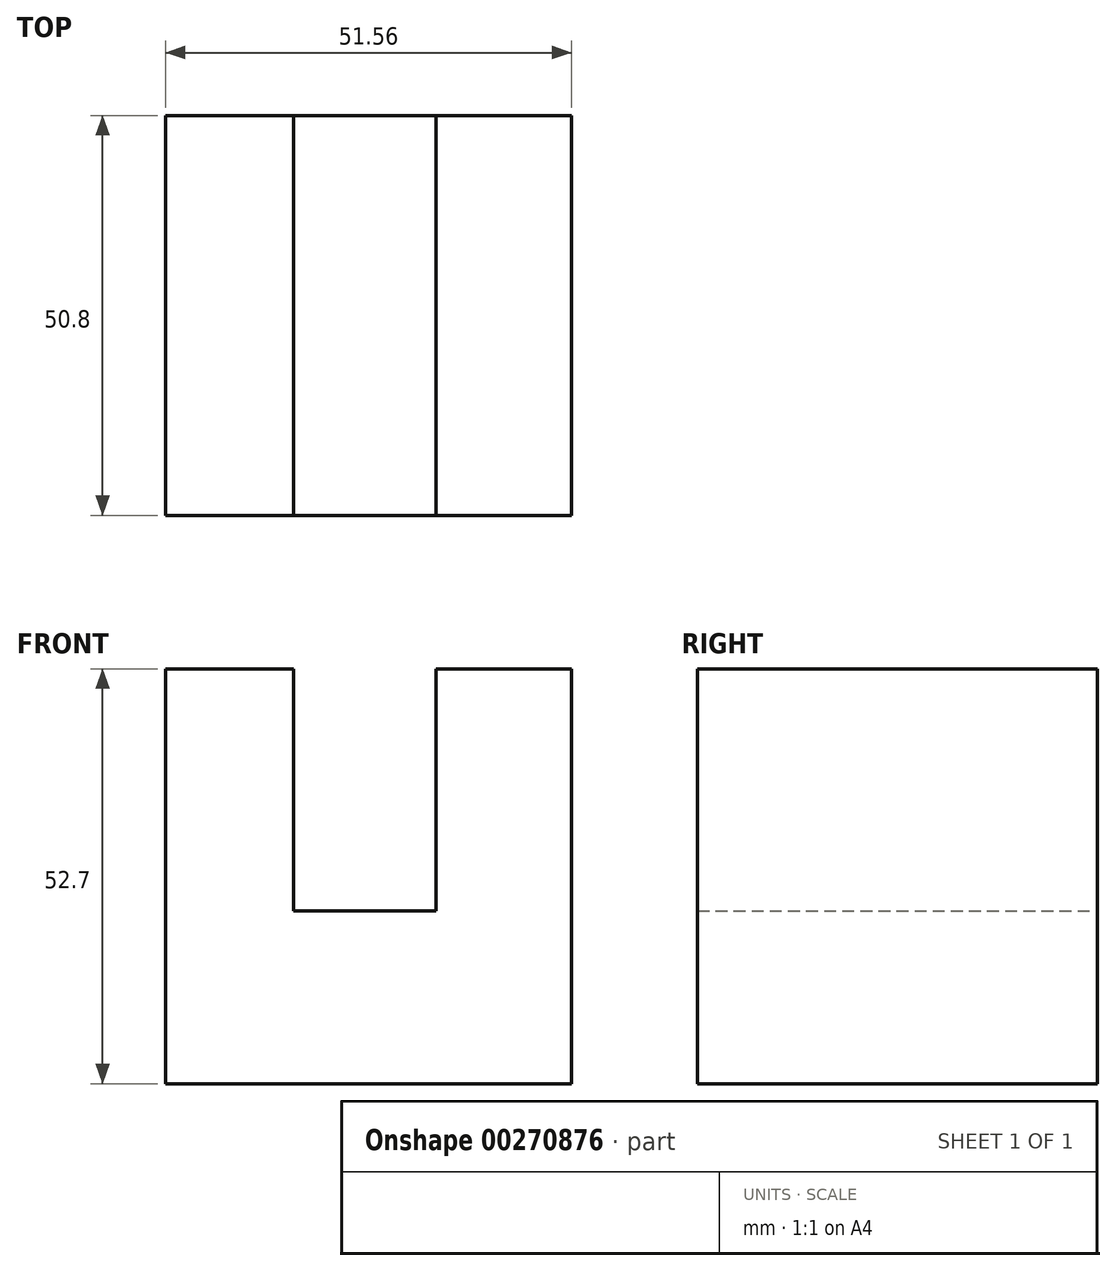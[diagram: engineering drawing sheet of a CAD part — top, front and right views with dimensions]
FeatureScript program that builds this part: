
annotation { "Feature Type Name" : "Feature", "Feature Type Description" : "" }
export const myFeature = defineFeature(function(context is Context, id is Id, definition is map)
    precondition{}
    {
        {
            var Q0;
            Q0=qCreatedBy(makeId("Front.planeOp"),FACE);
            var sketch = newSketch(context, id + "F0", { "sketchPlane" : qUnion([Q0])});
            skLineSegment(sketch, "E0.bottom", {"start": v(-55.19, 0) * mm, "end": v(-55.38, 0) * mm});
            skLineSegment(sketch, "E0.top", {"start": v(-55.19, 52.7) * mm, "end": v(-55.38, 52.7) * mm});
            skLineSegment(sketch, "E0.left", {"start": v(-55.19, 0) * mm, "end": v(-55.19, 52.7) * mm});
            skLineSegment(sketch, "E0.right", {"start": v(-55.38, 0) * mm, "end": v(-55.38, 52.7) * mm});
            skLineSegment(sketch, "E1.bottom", {"start": v(-55.19, 52.7) * mm, "end": v(-38.95, 52.7) * mm});
            skLineSegment(sketch, "E1.top", {"start": v(-55.19, 52.7) * mm, "end": v(-38.95, 52.7) * mm});
            skLineSegment(sketch, "E1.left", {"start": v(-55.19, 52.7) * mm, "end": v(-55.19, 52.7) * mm});
            skLineSegment(sketch, "E1.right", {"start": v(-38.95, 52.7) * mm, "end": v(-38.95, 52.7) * mm});
            skLineSegment(sketch, "E2.bottom", {"start": v(-38.95, 21.96) * mm, "end": v(-38.95, 21.96) * mm});
            skLineSegment(sketch, "E2.left", {"start": v(-38.95, 21.96) * mm, "end": v(-38.95, 52.7) * mm});
            skLineSegment(sketch, "E2.right", {"start": v(-38.95, 21.96) * mm, "end": v(-38.95, 52.7) * mm});
            skLineSegment(sketch, "E3.bottom", {"start": v(-38.95, 21.96) * mm, "end": v(-20.81, 21.96) * mm});
            skLineSegment(sketch, "E3.top", {"start": v(-38.95, 21.96) * mm, "end": v(-20.81, 21.96) * mm});
            skLineSegment(sketch, "E3.right", {"start": v(-20.81, 21.96) * mm, "end": v(-20.81, 21.96) * mm});
            skLineSegment(sketch, "E4.top", {"start": v(-20.81, 52.7) * mm, "end": v(-20.81, 52.7) * mm});
            skLineSegment(sketch, "E4.left", {"start": v(-20.81, 21.96) * mm, "end": v(-20.81, 52.7) * mm});
            skLineSegment(sketch, "E4.right", {"start": v(-20.81, 21.96) * mm, "end": v(-20.81, 52.7) * mm});
            skLineSegment(sketch, "E5.bottom", {"start": v(-3.63, 52.7) * mm, "end": v(-20.81, 52.7) * mm});
            skLineSegment(sketch, "E5.top", {"start": v(-3.63, 52.7) * mm, "end": v(-20.81, 52.7) * mm});
            skLineSegment(sketch, "E5.left", {"start": v(-3.63, 52.7) * mm, "end": v(-3.63, 52.7) * mm});
            skLineSegment(sketch, "E6.bottom", {"start": v(-3.63, 0) * mm, "end": v(-3.63, 0) * mm});
            skLineSegment(sketch, "E6.left", {"start": v(-3.63, 0) * mm, "end": v(-3.63, 52.7) * mm});
            skLineSegment(sketch, "E6.right", {"start": v(-3.63, 0) * mm, "end": v(-3.63, 52.7) * mm});
            skLineSegment(sketch, "E7", {"start": v(-55.38, 0) * mm, "end": v(-3.63, 0) * mm});
            skSolve(sketch);
        }
        {
            var Q0;
            Q0=qCreatedBy(makeId("Front.planeOp"),FACE);
            var sketch = newSketch(context, id + "F1", { "sketchPlane" : qUnion([Q0])});
            skLineSegment(sketch, "E8.bottom", {"start": v(-55.19, 0) * mm, "end": v(-3.44, 0) * mm});
            skLineSegment(sketch, "E8.top", {"start": v(-55.19, 0) * mm, "end": v(-3.44, 0) * mm});
            skLineSegment(sketch, "E8.left", {"start": v(-55.19, 0) * mm, "end": v(-55.19, 0) * mm});
            skLineSegment(sketch, "E8.right", {"start": v(-3.44, 0) * mm, "end": v(-3.44, 0) * mm});
            skSolve(sketch);
        }
        {
            var Q0;
            Q0 = qSketchRegion(id + "F1", true);
            var Q1;
            {var subQ1=sQuery(id+"F0.wireOp",EDGE,"E0.left");Q1=makeQuery(id+"F0.imprint","IMPRINT",FACE,{"disambiguationData":[TD([[makeQuery(id+"F0.imprint","IMPRINT",EDGE,{"derivedFrom":subQ1}),-1.0]])]});}
            extrude(context, id + "F2", {"entities" : qUnion([Q0, Q1]), "depth" : 50.8 * mm});
        }
    });
